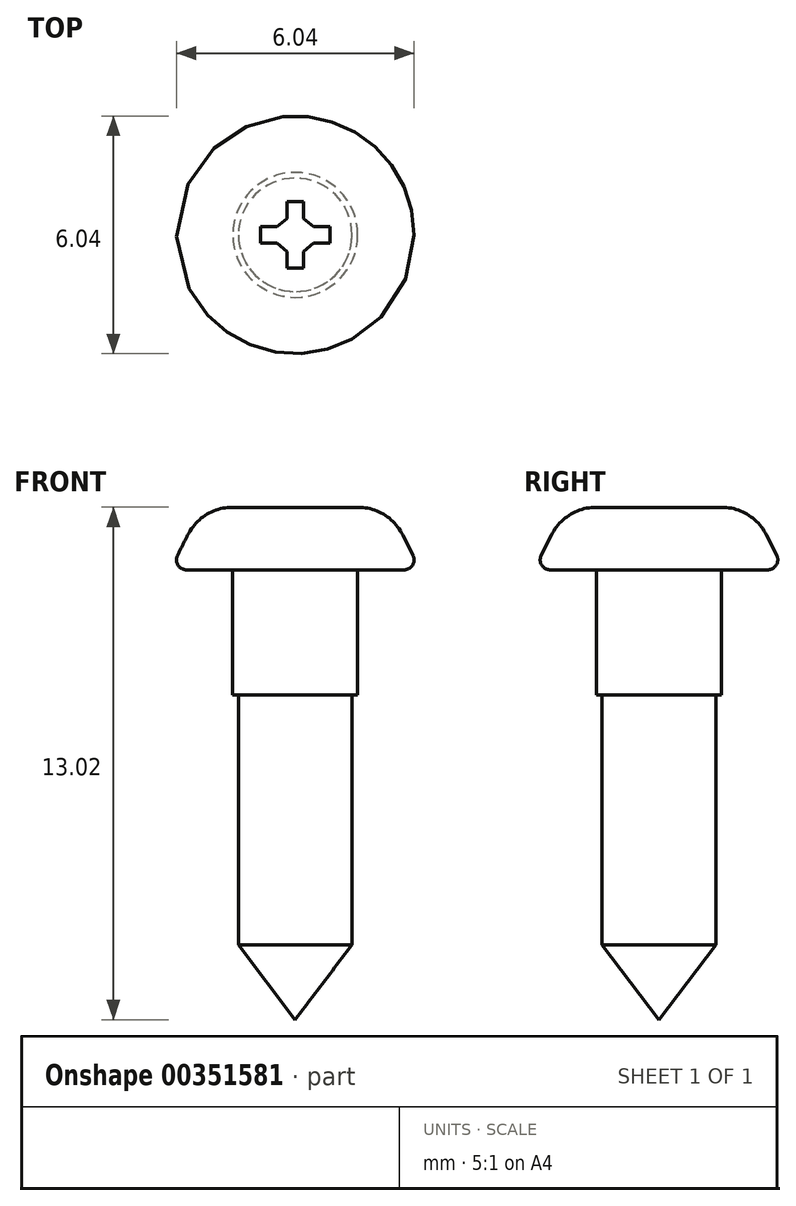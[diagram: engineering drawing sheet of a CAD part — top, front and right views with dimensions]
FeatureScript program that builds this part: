
annotation { "Feature Type Name" : "Feature", "Feature Type Description" : "" }
export const myFeature = defineFeature(function(context is Context, id is Id, definition is map)
    precondition{}
    {
        {
            var Q0;
            Q0=qCreatedBy(makeId("Top.planeOp"),FACE);
            var sketch = newSketch(context, id + "F0", { "sketchPlane" : qUnion([Q0])});
            skPoint(sketch, "E0.start.orphan", {"position": v(0, 1.51) * mm});
            skCircle(sketch, "E1", {"center": v(0, 0) * mm, "radius": 3.18 * mm});
            skSolve(sketch);
        }
        {
            var Q0;
            Q0=qCreatedBy(makeId("Top.planeOp"),FACE);
            cPlane(context, id + "F1", {"entities" : qUnion([Q0]), "cplaneType" : CPlaneType.OFFSET, "offset" : 1.59 * mm, "width" : 152.4 * mm, "height" : 152.4 * mm});
        }
        {
            var Q0;
            Q0=qCreatedBy(id+"F1.planeOp",FACE);
            var sketch = newSketch(context, id + "F2", { "sketchPlane" : qUnion([Q0])});
            skCircle(sketch, "E2", {"center": v(0, 0) * mm, "radius": 2.38 * mm});
            skSolve(sketch);
        }
        {
            var Q0;
            Q0 = qSketchRegion(id + "F0", true);
            var Q1;
            Q1 = qSketchRegion(id + "F2", true);
            loft(context, id + "F3", {"sheetProfilesArray" : [{ "sheetProfileEntities" : qUnion([Q0]) }, { "sheetProfileEntities" : qUnion([Q1]) }]});
        }
        {
            var Q0;
            Q0=makeQuery(id+"F3.opLoft","MID_CAP_EDGE",EDGE,{"disambiguationData":[OSD([sQuery(id+"F0.wireOp",EDGE,"E1"),sQuery(id+"F2.wireOp",EDGE,"E2")])],"capPos":1.0});
            fillet(context, id + "F4", {"entities" : qUnion([Q0]), "radius" : 1.27 * mm, "tangentPropagation" : true, "allowEdgeOverflow" : false});
        }
        {
            var Q0;
            Q0=makeQuery(id+"F3.opLoft","MID_CAP_EDGE",EDGE,{"disambiguationData":[OSD([sQuery(id+"F0.wireOp",EDGE,"E1")])],"capPos":0.0});
            fillet(context, id + "F5", {"entities" : qUnion([Q0]), "radius" : 0.25 * mm, "tangentPropagation" : true, "allowEdgeOverflow" : false});
        }
        {
            var Q0;
            Q0=makeQuery(id+"F3.opLoft","CAP_FACE",FACE,{"disambiguationData":[OSD([makeQuery(id+"F2.imprint","IMPRINT",FACE,{"disambiguationData":[TD([[makeQuery(id+"F2.imprint","IMPRINT",EDGE,{"derivedFrom":sQuery(id+"F2.wireOp",EDGE,"E2")}),1.0]])]})])],"isStart":true});
            var sketch = newSketch(context, id + "F6", { "sketchPlane" : qUnion([Q0])});
            skLineSegment(sketch, "E3", {"start": v(-0.21, 0.42) * mm, "end": v(-0.21, 0.84) * mm});
            skLineSegment(sketch, "E4", {"start": v(-0.21, 0.84) * mm, "end": v(0.21, 0.84) * mm});
            skLineSegment(sketch, "E5", {"start": v(0.21, 0.84) * mm, "end": v(0.21, 0.42) * mm});
            skLineSegment(sketch, "E6", {"start": v(0.21, 0.42) * mm, "end": v(0.46, 0.21) * mm});
            skLineSegment(sketch, "E7", {"start": v(0.46, 0.21) * mm, "end": v(0.89, 0.21) * mm});
            skLineSegment(sketch, "E8", {"start": v(0.89, 0.21) * mm, "end": v(0.89, -0.21) * mm});
            skLineSegment(sketch, "E9", {"start": v(0.89, -0.21) * mm, "end": v(0.46, -0.21) * mm});
            skLineSegment(sketch, "E10", {"start": v(0.46, -0.21) * mm, "end": v(0.21, -0.42) * mm});
            skLineSegment(sketch, "E11", {"start": v(0.21, -0.42) * mm, "end": v(0.21, -0.84) * mm});
            skLineSegment(sketch, "E12", {"start": v(0.21, -0.84) * mm, "end": v(-0.21, -0.84) * mm});
            skLineSegment(sketch, "E13", {"start": v(-0.21, -0.84) * mm, "end": v(-0.21, -0.42) * mm});
            skLineSegment(sketch, "E14", {"start": v(-0.21, -0.42) * mm, "end": v(-0.46, -0.21) * mm});
            skLineSegment(sketch, "E15", {"start": v(-0.46, -0.21) * mm, "end": v(-0.89, -0.21) * mm});
            skLineSegment(sketch, "E16", {"start": v(-0.89, -0.21) * mm, "end": v(-0.89, 0.21) * mm});
            skLineSegment(sketch, "E17", {"start": v(-0.89, 0.21) * mm, "end": v(-0.46, 0.21) * mm});
            skLineSegment(sketch, "E18", {"start": v(-0.46, 0.21) * mm, "end": v(-0.21, 0.42) * mm});
            skLineSegment(sketch, "E19", {"start": v(0, 1.4) * mm, "end": v(0, -1.45) * mm, "construction": true});
            skLineSegment(sketch, "E20", {"start": v(-1.17, 0) * mm, "end": v(1.51, 0) * mm, "construction": true});
            skSolve(sketch);
        }
        {
            var Q0;
            Q0 = qSketchRegion(id + "F6", true);
            extrude(context, id + "F7", {"entities" : qUnion([Q0]), "operationType" : NewBodyOperationType.REMOVE, "oppositeDirection" : true, "depth" : 1 / 406.4 * mm});
        }
        {
            var Q0;
            Q0=qCreatedBy(makeId("Top.planeOp"),FACE);
            var sketch = newSketch(context, id + "F8", { "sketchPlane" : qUnion([Q0])});
            skCircle(sketch, "E21", {"center": v(0, 0) * mm, "radius": 1.59 * mm});
            skSolve(sketch);
        }
        {
            var Q0;
            Q0 = qSketchRegion(id + "F8", true);
            extrude(context, id + "F9", {"entities" : qUnion([Q0]), "operationType" : NewBodyOperationType.ADD, "oppositeDirection" : true, "depth" : 3.17 * mm});
        }
        {
            var Q0;
            Q0=makeQuery(id+"F9.opExtrude","CAP_FACE",FACE,{"disambiguationData":[OSD([sQuery(id+"F8.wireOp",EDGE,"E21")])],"isStart":false});
            var sketch = newSketch(context, id + "F10", { "sketchPlane" : qUnion([Q0])});
            skCircle(sketch, "E22", {"center": v(0, 0) * mm, "radius": 1.44 * mm});
            skSolve(sketch);
        }
        {
            var Q0;
            Q0 = qSketchRegion(id + "F10", true);
            extrude(context, id + "F11", {"entities" : qUnion([Q0]), "operationType" : NewBodyOperationType.ADD, "depth" : 6.35 * mm});
        }
        {
            var Q0;
            Q0=qCreatedBy(makeId("Right.planeOp"),FACE);
            var sketch = newSketch(context, id + "F12", { "sketchPlane" : qUnion([Q0])});
            skLineSegment(sketch, "E23.0", {"start": v(1.44, -9.53) * mm, "end": v(-1.44, -9.53) * mm});
            skLineSegment(sketch, "E24", {"start": v(1.44, -3.18) * mm, "end": v(1.44, -9.53) * mm});
            skLineSegment(sketch, "E25", {"start": v(1.44, -9.53) * mm, "end": v(0, -11.43) * mm});
            skLineSegment(sketch, "E26", {"start": v(0, -11.43) * mm, "end": v(0, -9.53) * mm});
            skSolve(sketch);
        }
        {
            var Q0;
            Q0 = qSketchRegion(id + "F12", true);
            var Q1;
            Q1=sQuery(id+"F12.wireOp",EDGE,"E26");
            revolve(context, id + "F13", {"operationType" : NewBodyOperationType.ADD, "entities" : qUnion([Q0]), "axis" : qUnion([Q1]), "revolveType" : RevolveType.FULL});
        }
    });
